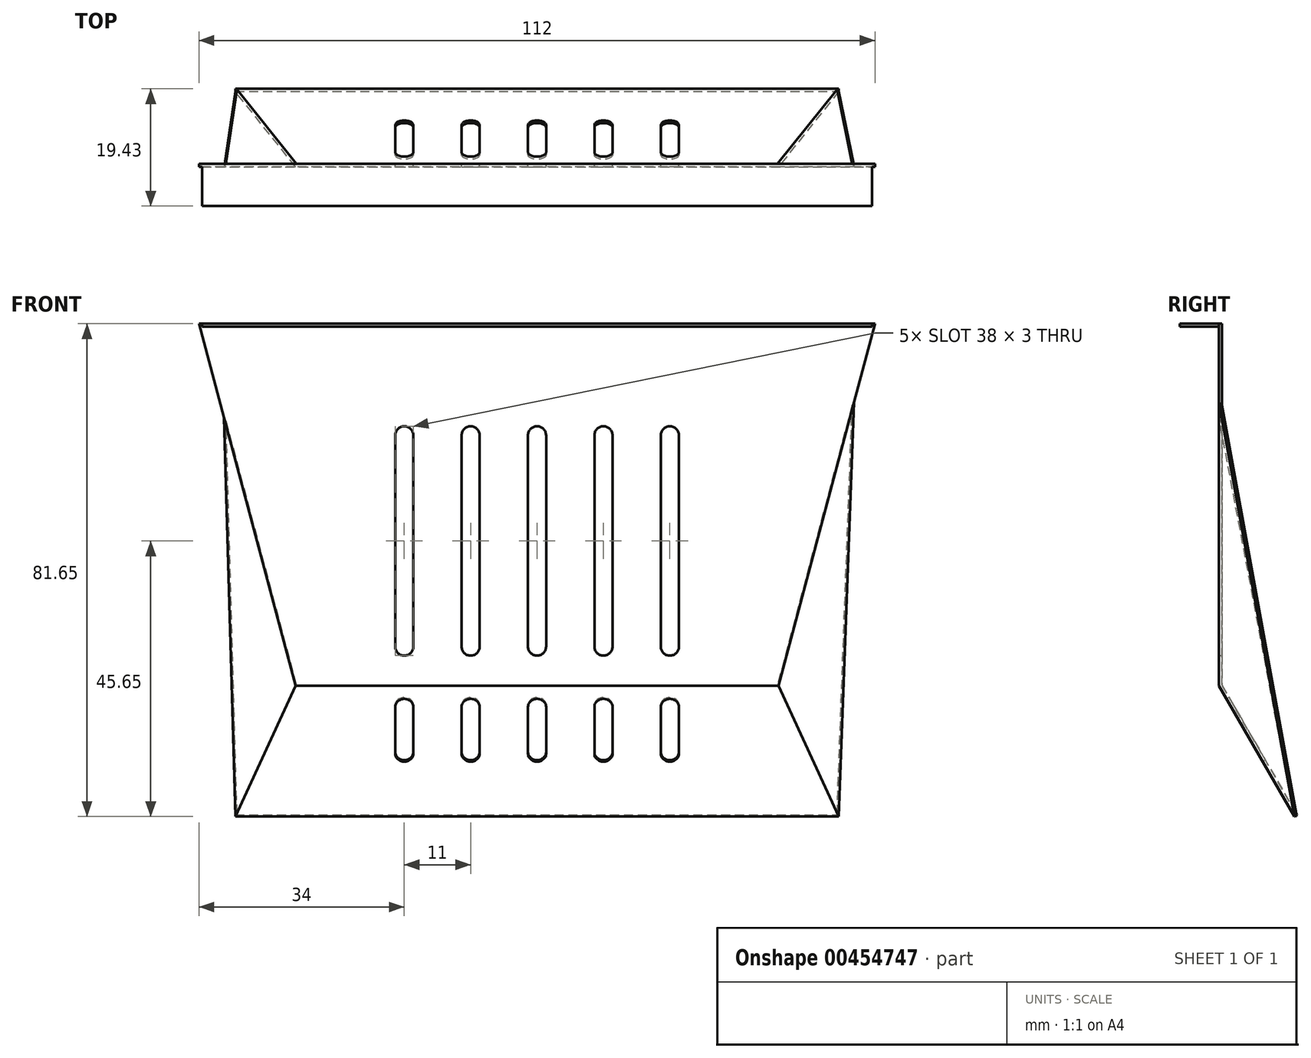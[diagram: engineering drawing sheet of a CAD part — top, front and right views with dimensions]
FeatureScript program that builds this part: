
annotation { "Feature Type Name" : "Feature", "Feature Type Description" : "" }
export const myFeature = defineFeature(function(context is Context, id is Id, definition is map)
    precondition{}
    {
        {
            var Q0;
            Q0=qCreatedBy(makeId("Front.planeOp"),FACE);
            var sketch = newSketch(context, id + "F0", { "sketchPlane" : qUnion([Q0])});
            skLineSegment(sketch, "E0", {"start": v(40, 0) * mm, "end": v(-40, 0) * mm});
            skLineSegment(sketch, "E1", {"start": v(-40, 0) * mm, "end": v(-56, 60) * mm});
            skLineSegment(sketch, "E2", {"start": v(-56, 60) * mm, "end": v(56, 60) * mm});
            skLineSegment(sketch, "E3", {"start": v(56, 60) * mm, "end": v(40, 0) * mm});
            skLineSegment(sketch, "E4.left", {"start": v(20.5, 41.5) * mm, "end": v(20.5, 6.5) * mm});
            skLineSegment(sketch, "E4.right", {"start": v(23.5, 41.5) * mm, "end": v(23.5, 6.5) * mm});
            skArc(sketch, "E5", {"start": v(20.5, 41.5) * mm, "mid": v(22, 43) * mm, "end": v(23.5, 41.5) * mm});
            skArc(sketch, "E6", {"start": v(23.5, 6.5) * mm, "mid": v(22, 5) * mm, "end": v(20.5, 6.5) * mm});
            skArc(sketch, "E7.1.0.0", {"start": v(12.5, 6.5) * mm, "mid": v(11, 5) * mm, "end": v(9.5, 6.5) * mm});
            skLineSegment(sketch, "E7.1.0.1", {"start": v(12.5, 41.5) * mm, "end": v(12.5, 6.5) * mm});
            skArc(sketch, "E7.1.0.2", {"start": v(9.5, 41.5) * mm, "mid": v(11, 43) * mm, "end": v(12.5, 41.5) * mm});
            skLineSegment(sketch, "E7.1.0.3", {"start": v(9.5, 41.5) * mm, "end": v(9.5, 6.5) * mm});
            skArc(sketch, "E7.2.0.0", {"start": v(1.5, 6.5) * mm, "mid": v(0, 5) * mm, "end": v(-1.5, 6.5) * mm});
            skLineSegment(sketch, "E7.2.0.1", {"start": v(1.5, 41.5) * mm, "end": v(1.5, 6.5) * mm});
            skArc(sketch, "E7.2.0.2", {"start": v(-1.5, 41.5) * mm, "mid": v(0, 43) * mm, "end": v(1.5, 41.5) * mm});
            skLineSegment(sketch, "E7.2.0.3", {"start": v(-1.5, 41.5) * mm, "end": v(-1.5, 6.5) * mm});
            skArc(sketch, "E7.3.0.0", {"start": v(-9.5, 6.5) * mm, "mid": v(-11, 5) * mm, "end": v(-12.5, 6.5) * mm});
            skLineSegment(sketch, "E7.3.0.1", {"start": v(-9.5, 41.5) * mm, "end": v(-9.5, 6.5) * mm});
            skArc(sketch, "E7.3.0.2", {"start": v(-12.5, 41.5) * mm, "mid": v(-11, 43) * mm, "end": v(-9.5, 41.5) * mm});
            skLineSegment(sketch, "E7.3.0.3", {"start": v(-12.5, 41.5) * mm, "end": v(-12.5, 6.5) * mm});
            skArc(sketch, "E7.4.0.0", {"start": v(-20.5, 6.5) * mm, "mid": v(-22, 5) * mm, "end": v(-23.5, 6.5) * mm});
            skLineSegment(sketch, "E7.4.0.1", {"start": v(-20.5, 41.5) * mm, "end": v(-20.5, 6.5) * mm});
            skArc(sketch, "E7.4.0.2", {"start": v(-23.5, 41.5) * mm, "mid": v(-22, 43) * mm, "end": v(-20.5, 41.5) * mm});
            skLineSegment(sketch, "E7.4.0.3", {"start": v(-23.5, 41.5) * mm, "end": v(-23.5, 6.5) * mm});
            skLineSegment(sketch, "E7.direction1", {"start": v(20.5, 6.5) * mm, "end": v(9.5, 6.5) * mm, "construction": true});
            skSolve(sketch);
        }
        {
            var Q0;
            Q0=makeQuery(id+"F0.imprint","IMPRINT",FACE,{"disambiguationData":[TD([[makeQuery(id+"F0.imprint","IMPRINT",EDGE,{"derivedFrom":sQuery(id+"F0.wireOp",EDGE,"E0")}),-1.0]])]});
            extrude(context, id + "F1", {"entities" : qUnion([Q0]), "depth" : 0.5 * mm});
        }
        {
            var Q0;
            Q0=makeQuery(id+"F1.opExtrude","CAP_FACE",FACE,{"disambiguationData":[OSD([sQuery(id+"F0.wireOp",EDGE,"E0"),sQuery(id+"F0.wireOp",EDGE,"E1"),sQuery(id+"F0.wireOp",EDGE,"E2"),sQuery(id+"F0.wireOp",EDGE,"E3"),sQuery(id+"F0.wireOp",EDGE,"E4.left"),sQuery(id+"F0.wireOp",EDGE,"E4.right"),sQuery(id+"F0.wireOp",EDGE,"E5"),sQuery(id+"F0.wireOp",EDGE,"E6"),sQuery(id+"F0.wireOp",EDGE,"E7.1.0.0"),sQuery(id+"F0.wireOp",EDGE,"E7.1.0.1"),sQuery(id+"F0.wireOp",EDGE,"E7.1.0.2"),sQuery(id+"F0.wireOp",EDGE,"E7.1.0.3"),sQuery(id+"F0.wireOp",EDGE,"E7.2.0.0"),sQuery(id+"F0.wireOp",EDGE,"E7.2.0.1"),sQuery(id+"F0.wireOp",EDGE,"E7.2.0.2"),sQuery(id+"F0.wireOp",EDGE,"E7.2.0.3"),sQuery(id+"F0.wireOp",EDGE,"E7.3.0.0"),sQuery(id+"F0.wireOp",EDGE,"E7.3.0.1"),sQuery(id+"F0.wireOp",EDGE,"E7.3.0.2"),sQuery(id+"F0.wireOp",EDGE,"E7.3.0.3"),sQuery(id+"F0.wireOp",EDGE,"E7.4.0.0"),sQuery(id+"F0.wireOp",EDGE,"E7.4.0.1"),sQuery(id+"F0.wireOp",EDGE,"E7.4.0.2"),sQuery(id+"F0.wireOp",EDGE,"E7.4.0.3")])],"isStart":false});
            var sketch = newSketch(context, id + "F2", { "sketchPlane" : qUnion([Q0])});
            skLineSegment(sketch, "E8.0", {"start": v(-55.5, 60) * mm, "end": v(55.5, 60) * mm});
            skLineSegment(sketch, "E9", {"start": v(-55.5, 60) * mm, "end": v(-55.5, 59.5) * mm});
            skLineSegment(sketch, "E10", {"start": v(-55.5, 59.5) * mm, "end": v(55.5, 59.5) * mm});
            skLineSegment(sketch, "E11", {"start": v(55.5, 59.5) * mm, "end": v(55.5, 60) * mm});
            skPoint(sketch, "E12.orphan", {"position": v(56, 60) * mm});
            skPoint(sketch, "E13.orphan", {"position": v(-56, 60) * mm});
            skSolve(sketch);
        }
        {
            var Q0;
            Q0 = qSketchRegion(id + "F2", true);
            extrude(context, id + "F3", {"entities" : qUnion([Q0]), "operationType" : NewBodyOperationType.ADD, "depth" : 6.5 * mm});
        }
        {
            var Q0;
            Q0=makeQuery(id+"F1.opExtrude","CAP_EDGE",EDGE,{"disambiguationData":[OSD([sQuery(id+"F0.wireOp",EDGE,"E0")])],"isStart":false});
            cPlane(context, id + "F4", {"entities" : qUnion([Q0]), "cplaneType" : CPlaneType.LINE_ANGLE, "offset" : 25 * mm, "angle" : 30 * degree, "oppositeDirection" : true, "width" : 150 * mm, "height" : 150 * mm});
        }
        {
            var Q0;
            Q0=qCreatedBy(id+"F4.planeOp",FACE);
            var sketch = newSketch(context, id + "F5", { "sketchPlane" : qUnion([Q0])});
            skLineSegment(sketch, "E14.0", {"start": v(40, 0.25) * mm, "end": v(-40, 0.25) * mm});
            skLineSegment(sketch, "E15", {"start": v(-40, 0.25) * mm, "end": v(-50, -24.75) * mm});
            skLineSegment(sketch, "E16", {"start": v(-50, -24.75) * mm, "end": v(50, -24.75) * mm});
            skLineSegment(sketch, "E17", {"start": v(50, -24.75) * mm, "end": v(40, 0.25) * mm});
            skLineSegment(sketch, "E18.bottom", {"start": v(-23.5, -3.75) * mm, "end": v(-20.5, -3.75) * mm});
            skLineSegment(sketch, "E18.top", {"start": v(-23.5, -12.75) * mm, "end": v(-20.5, -12.75) * mm});
            skLineSegment(sketch, "E18.left", {"start": v(-23.5, -3.75) * mm, "end": v(-23.5, -12.75) * mm});
            skLineSegment(sketch, "E18.right", {"start": v(-20.5, -3.75) * mm, "end": v(-20.5, -12.75) * mm});
            skArc(sketch, "E19", {"start": v(-23.5, -3.75) * mm, "mid": v(-22, -2.25) * mm, "end": v(-20.5, -3.75) * mm});
            skArc(sketch, "E20", {"start": v(-20.5, -12.75) * mm, "mid": v(-22, -14.25) * mm, "end": v(-23.5, -12.75) * mm});
            skLineSegment(sketch, "E21.1.0.0", {"start": v(-12.5, -12.75) * mm, "end": v(-9.5, -12.75) * mm});
            skLineSegment(sketch, "E21.1.0.1", {"start": v(-12.5, -3.75) * mm, "end": v(-9.5, -3.75) * mm});
            skLineSegment(sketch, "E21.1.0.2", {"start": v(-12.5, -3.75) * mm, "end": v(-12.5, -12.75) * mm});
            skLineSegment(sketch, "E21.1.0.3", {"start": v(-9.5, -3.75) * mm, "end": v(-9.5, -12.75) * mm});
            skArc(sketch, "E21.1.0.4", {"start": v(-12.5, -3.75) * mm, "mid": v(-11, -2.25) * mm, "end": v(-9.5, -3.75) * mm});
            skArc(sketch, "E21.1.0.5", {"start": v(-9.5, -12.75) * mm, "mid": v(-11, -14.25) * mm, "end": v(-12.5, -12.75) * mm});
            skLineSegment(sketch, "E21.2.0.0", {"start": v(-1.5, -12.75) * mm, "end": v(1.5, -12.75) * mm});
            skLineSegment(sketch, "E21.2.0.1", {"start": v(-1.5, -3.75) * mm, "end": v(1.5, -3.75) * mm});
            skLineSegment(sketch, "E21.2.0.2", {"start": v(-1.5, -3.75) * mm, "end": v(-1.5, -12.75) * mm});
            skLineSegment(sketch, "E21.2.0.3", {"start": v(1.5, -3.75) * mm, "end": v(1.5, -12.75) * mm});
            skArc(sketch, "E21.2.0.4", {"start": v(-1.5, -3.75) * mm, "mid": v(0, -2.25) * mm, "end": v(1.5, -3.75) * mm});
            skArc(sketch, "E21.2.0.5", {"start": v(1.5, -12.75) * mm, "mid": v(0, -14.25) * mm, "end": v(-1.5, -12.75) * mm});
            skLineSegment(sketch, "E21.3.0.0", {"start": v(9.5, -12.75) * mm, "end": v(12.5, -12.75) * mm});
            skLineSegment(sketch, "E21.3.0.1", {"start": v(9.5, -3.75) * mm, "end": v(12.5, -3.75) * mm});
            skLineSegment(sketch, "E21.3.0.2", {"start": v(9.5, -3.75) * mm, "end": v(9.5, -12.75) * mm});
            skLineSegment(sketch, "E21.3.0.3", {"start": v(12.5, -3.75) * mm, "end": v(12.5, -12.75) * mm});
            skArc(sketch, "E21.3.0.4", {"start": v(9.5, -3.75) * mm, "mid": v(11, -2.25) * mm, "end": v(12.5, -3.75) * mm});
            skArc(sketch, "E21.3.0.5", {"start": v(12.5, -12.75) * mm, "mid": v(11, -14.25) * mm, "end": v(9.5, -12.75) * mm});
            skLineSegment(sketch, "E21.4.0.0", {"start": v(20.5, -12.75) * mm, "end": v(23.5, -12.75) * mm});
            skLineSegment(sketch, "E21.4.0.1", {"start": v(20.5, -3.75) * mm, "end": v(23.5, -3.75) * mm});
            skLineSegment(sketch, "E21.4.0.2", {"start": v(20.5, -3.75) * mm, "end": v(20.5, -12.75) * mm});
            skLineSegment(sketch, "E21.4.0.3", {"start": v(23.5, -3.75) * mm, "end": v(23.5, -12.75) * mm});
            skArc(sketch, "E21.4.0.4", {"start": v(20.5, -3.75) * mm, "mid": v(22, -2.25) * mm, "end": v(23.5, -3.75) * mm});
            skArc(sketch, "E21.4.0.5", {"start": v(23.5, -12.75) * mm, "mid": v(22, -14.25) * mm, "end": v(20.5, -12.75) * mm});
            skLineSegment(sketch, "E21.direction1", {"start": v(-23.5, -12.75) * mm, "end": v(-12.5, -12.75) * mm, "construction": true});
            skSolve(sketch);
        }
        {
            var Q0;
            Q0=makeQuery(id+"F5.imprint","IMPRINT",FACE,{"disambiguationData":[TD([[makeQuery(id+"F5.imprint","IMPRINT",EDGE,{"derivedFrom":sQuery(id+"F5.wireOp",EDGE,"E14.0")}),1.0]])]});
            extrude(context, id + "F6", {"entities" : qUnion([Q0]), "operationType" : NewBodyOperationType.ADD, "oppositeDirection" : true, "depth" : 0.5 * mm});
        }
        {
            var Q0;
            Q0=makeQuery(id+"F1.opExtrude","CAP_VERTEX",VERTEX,{"disambiguationData":[OSD([sQuery(id+"F0.wireOp",EDGE,"E2"),sQuery(id+"F0.wireOp",EDGE,"E3")])],"isStart":false});
            var Q1;
            Q1=makeQuery(id+"F6.boolean.opBoolean","MERGE",VERTEX,{"derivedFrom":[makeQuery(id+"F1.opExtrude","CAP_VERTEX",VERTEX,{"disambiguationData":[OSD([sQuery(id+"F0.wireOp",EDGE,"E0"),sQuery(id+"F0.wireOp",EDGE,"E3")])],"isStart":false}),makeQuery(id+"F6.opExtrude","CAP_VERTEX",VERTEX,{"disambiguationData":[OSD([sQuery(id+"F5.wireOp",EDGE,"E14.0"),sQuery(id+"F5.wireOp",EDGE,"E17")])],"isStart":true})]});
            var Q2;
            Q2=makeQuery(id+"F6.opExtrude","CAP_VERTEX",VERTEX,{"disambiguationData":[OSD([sQuery(id+"F5.wireOp",EDGE,"E16"),sQuery(id+"F5.wireOp",EDGE,"E17")])],"isStart":true});
            cPlane(context, id + "F7", {"entities" : qUnion([Q0, Q1, Q2]), "cplaneType" : CPlaneType.THREE_POINT, "offset" : 25 * mm, "width" : 150 * mm, "height" : 150 * mm});
        }
        {
            var Q0;
            Q0=qCreatedBy(id+"F7.planeOp",FACE);
            var sketch = newSketch(context, id + "F8", { "sketchPlane" : qUnion([Q0])});
            skLineSegment(sketch, "E22.0", {"start": v(-43.97, -23.66) * mm, "end": v(-31.31, 0.1) * mm});
            skLineSegment(sketch, "E23.0", {"start": v(-47.18, 46.1) * mm, "end": v(-31.31, 0.1) * mm});
            skLineSegment(sketch, "E24", {"start": v(-43.97, -23.66) * mm, "end": v(-47.18, 46.1) * mm});
            skPoint(sketch, "E25.orphan", {"position": v(-51.56, 58.8) * mm});
            skSolve(sketch);
        }
        {
            var Q0;
            Q0=makeQuery(id+"F8.imprint","IMPRINT",FACE,{"disambiguationData":[TD([[makeQuery(id+"F8.imprint","IMPRINT",EDGE,{"derivedFrom":sQuery(id+"F8.wireOp",EDGE,"E22.0")}),1.0]])]});
            extrude(context, id + "F9", {"entities" : qUnion([Q0]), "operationType" : NewBodyOperationType.ADD, "depth" : 0.5 * mm});
        }
        {
            var Q0;
            Q0=makeQuery(id+"F6.boolean.opBoolean","MERGE",VERTEX,{"derivedFrom":[makeQuery(id+"F1.opExtrude","CAP_VERTEX",VERTEX,{"disambiguationData":[OSD([sQuery(id+"F0.wireOp",EDGE,"E0"),sQuery(id+"F0.wireOp",EDGE,"E1")])],"isStart":false}),makeQuery(id+"F6.opExtrude","CAP_VERTEX",VERTEX,{"disambiguationData":[OSD([sQuery(id+"F5.wireOp",EDGE,"E14.0"),sQuery(id+"F5.wireOp",EDGE,"E15")])],"isStart":true})]});
            var Q1;
            Q1=makeQuery(id+"F1.opExtrude","CAP_VERTEX",VERTEX,{"disambiguationData":[OSD([sQuery(id+"F0.wireOp",EDGE,"E1"),sQuery(id+"F0.wireOp",EDGE,"E2")])],"isStart":false});
            var Q2;
            Q2=makeQuery(id+"F6.opExtrude","CAP_VERTEX",VERTEX,{"disambiguationData":[OSD([sQuery(id+"F5.wireOp",EDGE,"E15"),sQuery(id+"F5.wireOp",EDGE,"E16")])],"isStart":true});
            cPlane(context, id + "F10", {"entities" : qUnion([Q0, Q1, Q2]), "cplaneType" : CPlaneType.THREE_POINT, "offset" : 25 * mm, "width" : 150 * mm, "height" : 150 * mm});
        }
        {
            var Q0;
            Q0=qCreatedBy(id+"F10.planeOp",FACE);
            var sketch = newSketch(context, id + "F11", { "sketchPlane" : qUnion([Q0])});
            skLineSegment(sketch, "E26.0", {"start": v(31.31, 0.1) * mm, "end": v(43.97, -23.66) * mm});
            skLineSegment(sketch, "E26.1", {"start": v(31.31, 0.1) * mm, "end": v(46.3, 43.59) * mm});
            skLineSegment(sketch, "E27", {"start": v(43.97, -23.66) * mm, "end": v(46.3, 43.59) * mm});
            skPoint(sketch, "E28.orphan", {"position": v(51.56, 58.8) * mm});
            skSolve(sketch);
        }
        {
            var Q0;
            Q0 = qSketchRegion(id + "F11", true);
            var Q1;
            Q1=sQuery(id+"F11.wireOp",EDGE,"E27");
            extrude(context, id + "F12", {"entities" : qUnion([Q0]), "operationType" : NewBodyOperationType.ADD, "surfaceEntities" : qUnion([Q1]), "depth" : 0.5 * mm});
        }
    });
